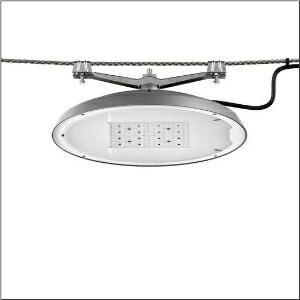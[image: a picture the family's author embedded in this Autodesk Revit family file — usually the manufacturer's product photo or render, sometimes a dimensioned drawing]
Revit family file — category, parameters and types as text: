
# Revit family: dl_r__50_iq_mini___st1_0s_5xa248w41f08le_08ea
name_source: partatom
category: Lighting Fixtures
units: mm (PartAtom-declared; Revit-internal decimal feet)

## family parameters
Cut with Voids When Loaded = No
Host = Face
Light Source = No
Part Type = Normal
Room Calculation Point = No
Round Connector Dimension = Use Diameter
Shared = No

## types (1)
- --- (1 x LED, 10390 lm, 64.1 W, 4000K)
    Apparent Load = 64 VA
    CIE Flux Codes = 37 72 97 100 100
    Color Rendering = 70
    Color Temperature = 4000K
    Default Elevation = 1800 mm
    Description = DL® 50 iQ mini, catenary luminaire, primary light control with lens, of PMMA, primary optical cover: cover, of toughened safety glass, transparent, light distribution: ST1.0s, light emission: direct distribution, primary light characteristic: symmetric, installation type: suspended mounting, LED, High Power LED, rated luminous flux: 10.390lm, luminous efficacy: 162lm/W, light colour: 740, colour temperature: 4000K, control gear: iQ Street-Remote, control: optimised constant luminous flux control (CLO 2.0), Desk-Remote (wireless, voltage-free reading and setting of iQ features in the workshop via application-optimized NFC function/RFID function), Light-Fading, Smart-Wire, Night-Set, Lumen-Switch, Temp-Guard, Auto-Match, Street-Remote, mains connection: 230..240V, AC, 50/60Hz, start of lifetime: 64W, end of service life: 67W, reduction: 30W, luminaire housing, of diecast aluminium, powder-coated, Siteco® metallic grey (DB 702S), diameter: 500mm, height: 115mm, mounting height: 4..12m, protection rating (complete): IP66, insulation class (complete): insulation class II (safety insulation), certification: CE, ENEC, ENEC+, VDE, impact resistance: IK08, permissible operating ambient temperature for outdoor applications: -25..+40°C, standard-compliant lighting for roads and squares, packaging unit: 1 piece

Light Distribution: ST1.0s
    Height = 124 mm  [stored 0.406824 ft]
    Lamp = 1 x LED
    Lamp Light Flux = 10390 lm
    Lamp Power = 64.1 W
    Lamp count = 1
    Length = 500 mm
    Luminous efficacy = 162 lm/W
    Manufacturer = Siteco
    ModVariant = No
    Model = 5XA248W41F08LE
    Number of Poles = 1
    OnlyDefault = Yes
    Power Factor = 1
    Product Name = DL® 50 iQ mini | ST1.0s
    Product group = catenary luminaire
    ProductGroupID = 6300
    Protection Class = Protection class II
    Protection Degree = IP 66
    RLX_Detail_Level = 1
    RLX_Emergency_Light_Flux = 0 lm
    RLX_Emergency_Type = 0
    RLX_Emergency_Type_DB = No
    RlxData = <blob elided: 127049 chars, md5=cf5f9935>
    Socket = socket
    Standby Power = 0 W
    System Light Flux = 10390 lm
    System Power = 64 W
    Type Comments = factory setting: luminous flux: 100 % | dim-lin: 254 | 672 mA
    Type Image = l_1251783.jpg
    URL = http://relux.com
    VarID = @adj_137918
    Voltage = 0 V
    Weight = 0.00 kg
    Width = 0 mm  [stored 0 ft]

note: [stored X ft] marks values corroborated as IEEE doubles in the binary element streams (Revit-internal decimal feet)

## geometry (parser evidence)
native form markers: Blend x4, Sweep x15
no freeform markers — native parametric forms only
